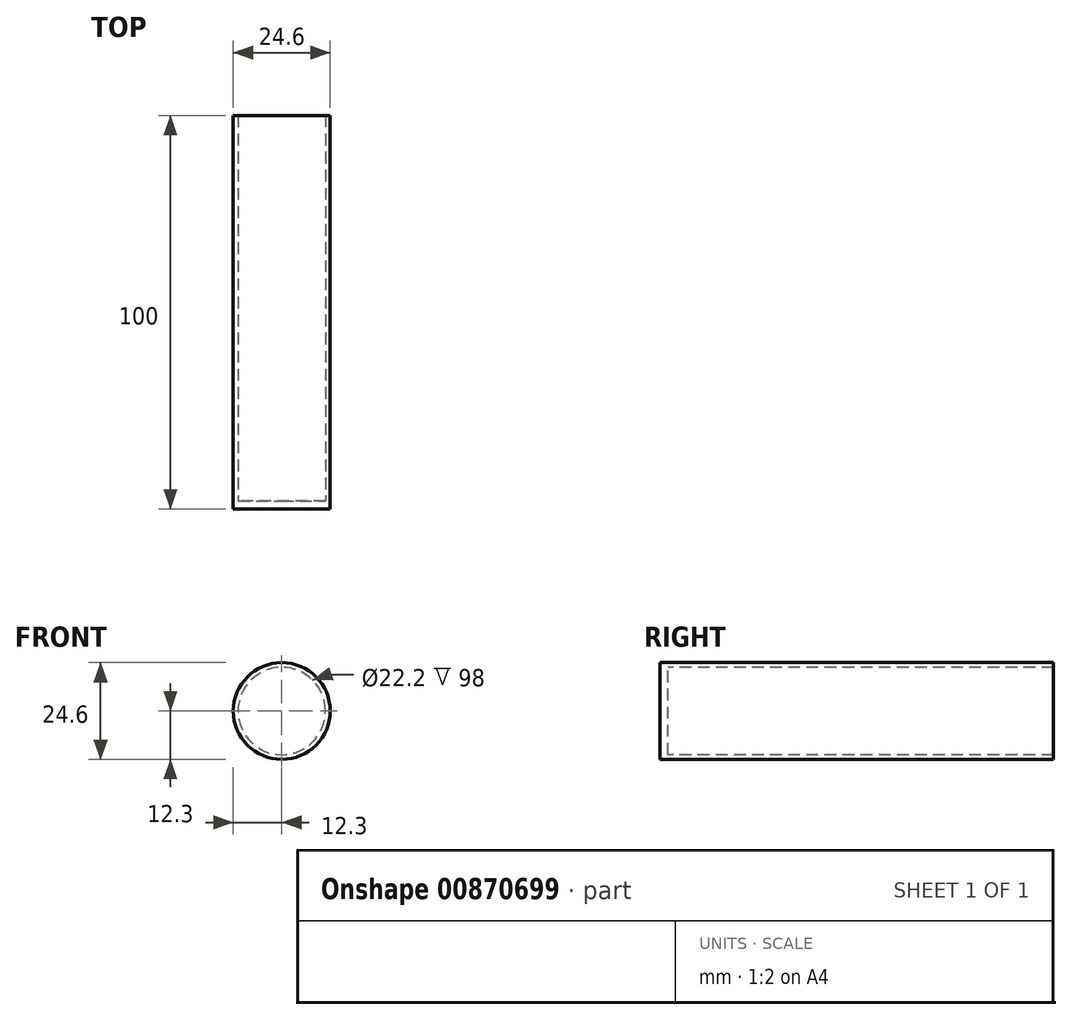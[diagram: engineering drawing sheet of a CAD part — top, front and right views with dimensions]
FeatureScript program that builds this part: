
annotation { "Feature Type Name" : "Feature", "Feature Type Description" : "" }
export const myFeature = defineFeature(function(context is Context, id is Id, definition is map)
    precondition{}
    {
        {
            var Q0;
            Q0=qCreatedBy(makeId("Front.planeOp"),FACE);
            var sketch = newSketch(context, id + "F0", { "sketchPlane" : qUnion([Q0])});
            skCircle(sketch, "E0", {"center": v(0, 0) * mm, "radius": 12.3 * mm});
            skCircle(sketch, "E1", {"center": v(0, 0) * mm, "radius": 11.1 * mm});
            skSolve(sketch);
        }
        {
            var Q0;
            Q0=qSketchRegion(id+"F0",true);
            extrude(context, id + "F1", {"entities" : qUnion([Q0]), "oppositeDirection" : true, "depth" : 100 * mm, "offsetDistance" : 25 * mm});
        }
        {
            var Q0;
            Q0=makeQuery(id+"F0.imprint","IMPRINT",FACE,{"disambiguationData":[TD([[makeQuery(id+"F0.imprint","IMPRINT",EDGE,{"derivedFrom":sQuery(id+"F0.wireOp",EDGE,"E1")}),1.0]])]});
            extrude(context, id + "F2", {"entities" : qUnion([Q0]), "operationType" : NewBodyOperationType.ADD, "oppositeDirection" : true, "depth" : 2 * mm, "offsetDistance" : 25 * mm});
        }
    });
